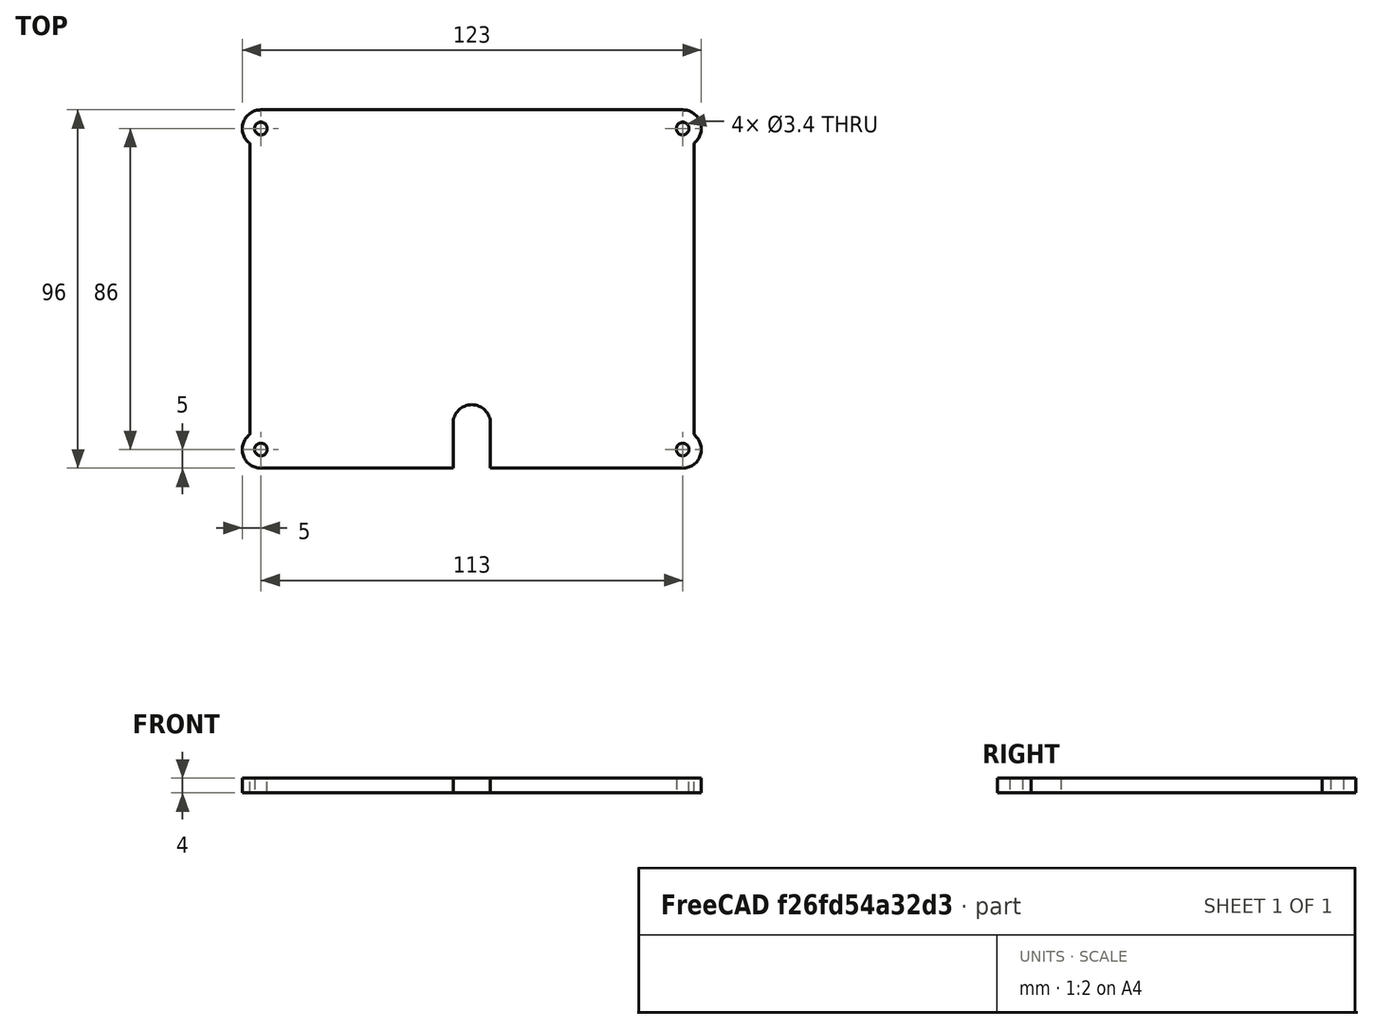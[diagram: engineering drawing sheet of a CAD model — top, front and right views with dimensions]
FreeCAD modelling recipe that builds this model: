
FCSTD DOCUMENT  (FreeCAD 0.21R33668 +7 (Git))
Label: 3_Head_Main
License: All rights reserved
LicenseURL: https://en.wikipedia.org/wiki/All_rights_reserved
objects: Sketcher::SketchObject×1, PartDesign::Pad×1, PartDesign::Body×1
note: 4 computed .brp shape members not serialized (recipe doc carries the construction recipe); baked Part::Feature solids carry a one-line shape summary decoded from their .brp

FEATURE [Sketcher::SketchObject] Sketch
  FullyConstrained = true
  MapMode = 5
  Support = -> [XY_Plane]
  sketch-geometry (20):
    g0: LineSegment StartX=-56.5 StartY=-43 StartZ=0 EndX=56.5 EndY=-43 EndZ=0
    g1: LineSegment StartX=56.5 StartY=-43 StartZ=0 EndX=56.5 EndY=43 EndZ=0
    g2: LineSegment StartX=56.5 StartY=43 StartZ=0 EndX=-56.5 EndY=43 EndZ=0
    g3: LineSegment StartX=-56.5 StartY=43 StartZ=0 EndX=-56.5 EndY=-43 EndZ=0
    g4: Circle CenterX=-56.5 CenterY=43 CenterZ=0 NormalX=0 NormalY=0 NormalZ=1 AngleXU=0 Radius=1.7
    g5: Circle CenterX=56.5 CenterY=43 CenterZ=0 NormalX=0 NormalY=0 NormalZ=1 AngleXU=0 Radius=1.7
    g6: Circle CenterX=-56.5 CenterY=-43 CenterZ=0 NormalX=0 NormalY=0 NormalZ=1 AngleXU=0 Radius=1.7
    g7: Circle CenterX=56.5 CenterY=-43 CenterZ=0 NormalX=0 NormalY=0 NormalZ=1 AngleXU=0 Radius=1.7
    g8: LineSegment StartX=-56.5 StartY=48 StartZ=0 EndX=56.5 EndY=48 EndZ=0
    g9: LineSegment StartX=-56.5 StartY=-48 StartZ=0 EndX=-5 EndY=-48 EndZ=0
    g10: LineSegment StartX=59.5 StartY=39 StartZ=0 EndX=59.5 EndY=-39 EndZ=0
    g11: LineSegment StartX=-59.5 StartY=39 StartZ=0 EndX=-59.5 EndY=-39 EndZ=0
    g12: ArcOfCircle CenterX=56.5 CenterY=43 CenterZ=0 NormalX=0 NormalY=0 NormalZ=1 AngleXU=0 Radius=5 StartAngle=5.35589 EndAngle=7.85398
    g13: ArcOfCircle CenterX=-56.5 CenterY=43 CenterZ=0 NormalX=0 NormalY=0 NormalZ=1 AngleXU=0 Radius=5 StartAngle=1.57079 EndAngle=4.06889
    g14: ArcOfCircle CenterX=-56.5 CenterY=-43 CenterZ=0 NormalX=0 NormalY=0 NormalZ=1 AngleXU=0 Radius=5 StartAngle=2.2143 EndAngle=4.71239
    g15: ArcOfCircle CenterX=56.5 CenterY=-43 CenterZ=0 NormalX=0 NormalY=0 NormalZ=1 AngleXU=0 Radius=5 StartAngle=4.71239 EndAngle=7.21048
    g16: LineSegment StartX=-5 StartY=-48 StartZ=0 EndX=-5 EndY=-36 EndZ=0
    g17: LineSegment StartX=5 StartY=-48 StartZ=0 EndX=5 EndY=-36 EndZ=0
    g18: ArcOfCircle CenterX=-1e-16 CenterY=-36 CenterZ=0 NormalX=0 NormalY=0 NormalZ=1 AngleXU=0 Radius=5 StartAngle=3.99229e-09 EndAngle=3.14159
    g19: LineSegment StartX=5 StartY=-48 StartZ=0 EndX=56.5 EndY=-48 EndZ=0
  constraints (51):
    c: Coincident(g0,g1)
    c: Coincident(g1,g2)
    c: Coincident(g2,g3)
    c: Coincident(g3,g0)
    c: Horizontal(g0)
    c: Horizontal(g2)
    c: Vertical(g1)
    c: Vertical(g3)
    c: Symmetric(g1,g0,g-1)
    c: DistanceX(g2,g2) = 113
    c: DistanceY(g3,g3) = 86
    c: Equal(g4,g5)
    c: Equal(g5,g6)
    c: Equal(g6,g7)
    c: Coincident(g4,g2)
    c: Coincident(g5,g1)
    c: Coincident(g6,g0)
    c: Coincident(g7,g0)
    c: Diameter(g4) = 3.4
    c: Horizontal(g8)
    c: Horizontal(g9)
    c: Vertical(g10)
    c: Coincident(g12,g10)
    c: Coincident(g13,g11)
    c: Coincident(g13,g8)
    c: Coincident(g14,g11)
    c: Coincident(g15,g10)
    c: Coincident(g12,g5)
    c: Coincident(g13,g4)
    c: Coincident(g14,g6)
    c: Coincident(g7,g15)
    c: Tangent(g12,g8) = 1.5708
    c: Equal(g13,g14)
    c: Equal(g12,g15)
    c: Radius(g13) = 5
    c: DistanceX(g11,g10) = 119
    c: Symmetric(g10,g11,g-1)
    c: Vertical(g11)
    c: Vertical(g16)
    c: Vertical(g17)
    c: Coincident(g18,g16)
    c: Coincident(g18,g17)
    c: Symmetric(g16,g17,g-2)
    c: DistanceX(g16,g17) = 10
    c: Radius(g18) = 5
    c: DistanceY(g17,g17) = 12
    c: Coincident(g9,g16)
    c: Coincident(g19,g17)
    c: Horizontal(g9,g17)
    c: Tangent(g14,g9) = -1.5708
    c: Tangent(g15,g19) = -1.5708
FEATURE [PartDesign::Pad] Pad
  Direction = (0,0,1)
  Length = 4
  Length2 = 10
  Profile = -> Sketch
  ReferenceAxis = -> Sketch [N_Axis]
  Type = 0
FEATURE [PartDesign::Body] Body
  Group = -> [Sketch,Pad]
  Origin = -> Origin
  Tip = -> Pad
